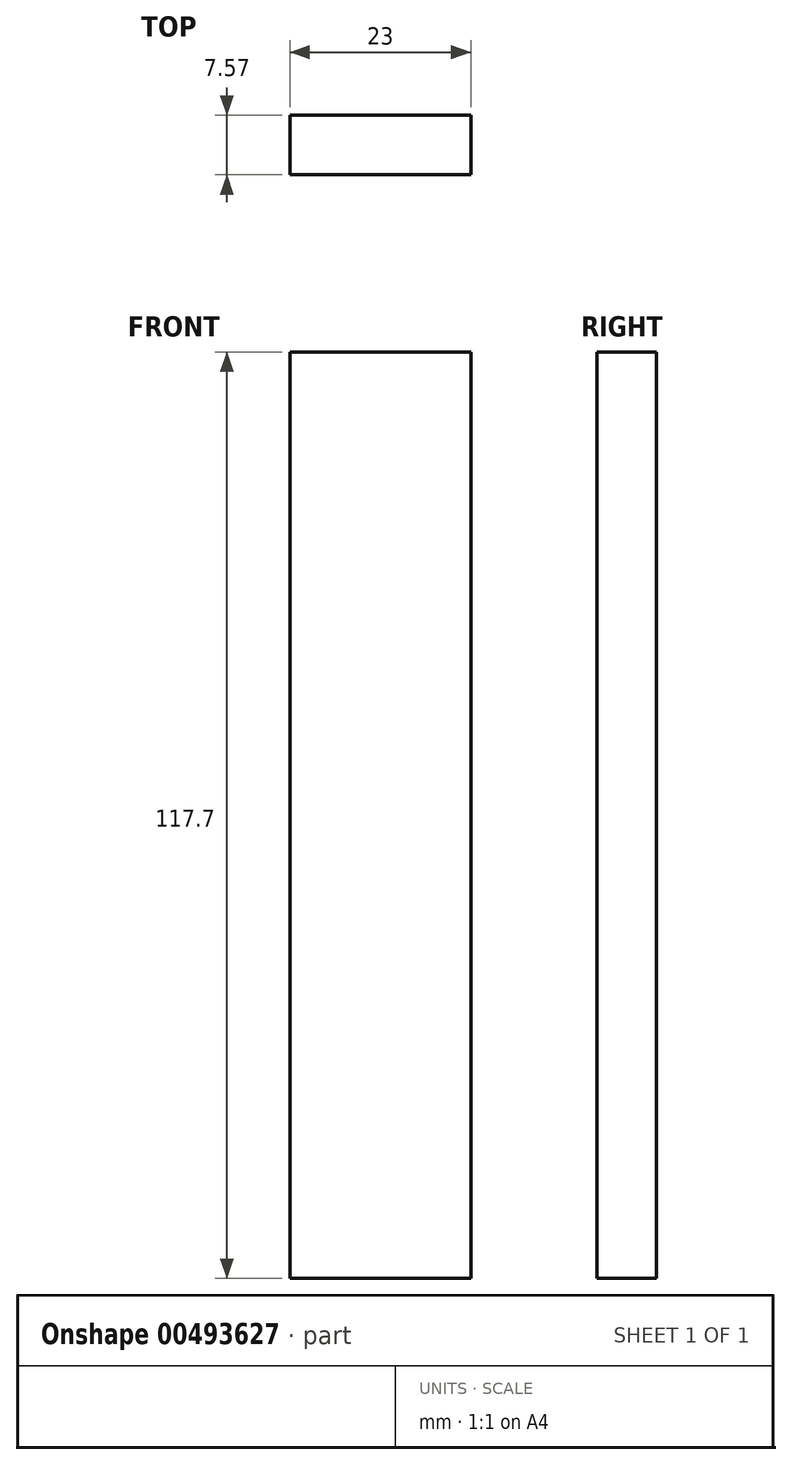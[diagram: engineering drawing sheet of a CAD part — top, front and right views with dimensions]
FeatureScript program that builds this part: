
annotation { "Feature Type Name" : "Feature", "Feature Type Description" : "" }
export const myFeature = defineFeature(function(context is Context, id is Id, definition is map)
    precondition{}
    {
        {
            var Q0;
            Q0=qCreatedBy(makeId("Front.planeOp"),FACE);
            var sketch = newSketch(context, id + "F0", { "sketchPlane" : qUnion([Q0])});
            skLineSegment(sketch, "E0.bottom", {"start": v(12.1, 58.85) * mm, "end": v(-10.9, 58.85) * mm});
            skLineSegment(sketch, "E0.top", {"start": v(12.1, -58.85) * mm, "end": v(-10.9, -58.85) * mm});
            skLineSegment(sketch, "E0.left", {"start": v(12.1, 58.85) * mm, "end": v(12.1, -58.85) * mm});
            skLineSegment(sketch, "E0.right", {"start": v(-10.9, 58.85) * mm, "end": v(-10.9, -58.85) * mm});
            skPoint(sketch, "E0.middle", {"position": v(0.6, 0) * mm});
            skSolve(sketch);
        }
        {
            var Q0;
            Q0=makeQuery(id+"F0.imprint","IMPRINT",FACE,{"disambiguationData":[TD([[makeQuery(id+"F0.imprint","IMPRINT",EDGE,{"derivedFrom":sQuery(id+"F0.wireOp",EDGE,"E0.bottom")}),1.0]])]});
            extrude(context, id + "F1", {"entities" : qUnion([Q0]), "depth" : 7.57 * mm});
        }
    });
